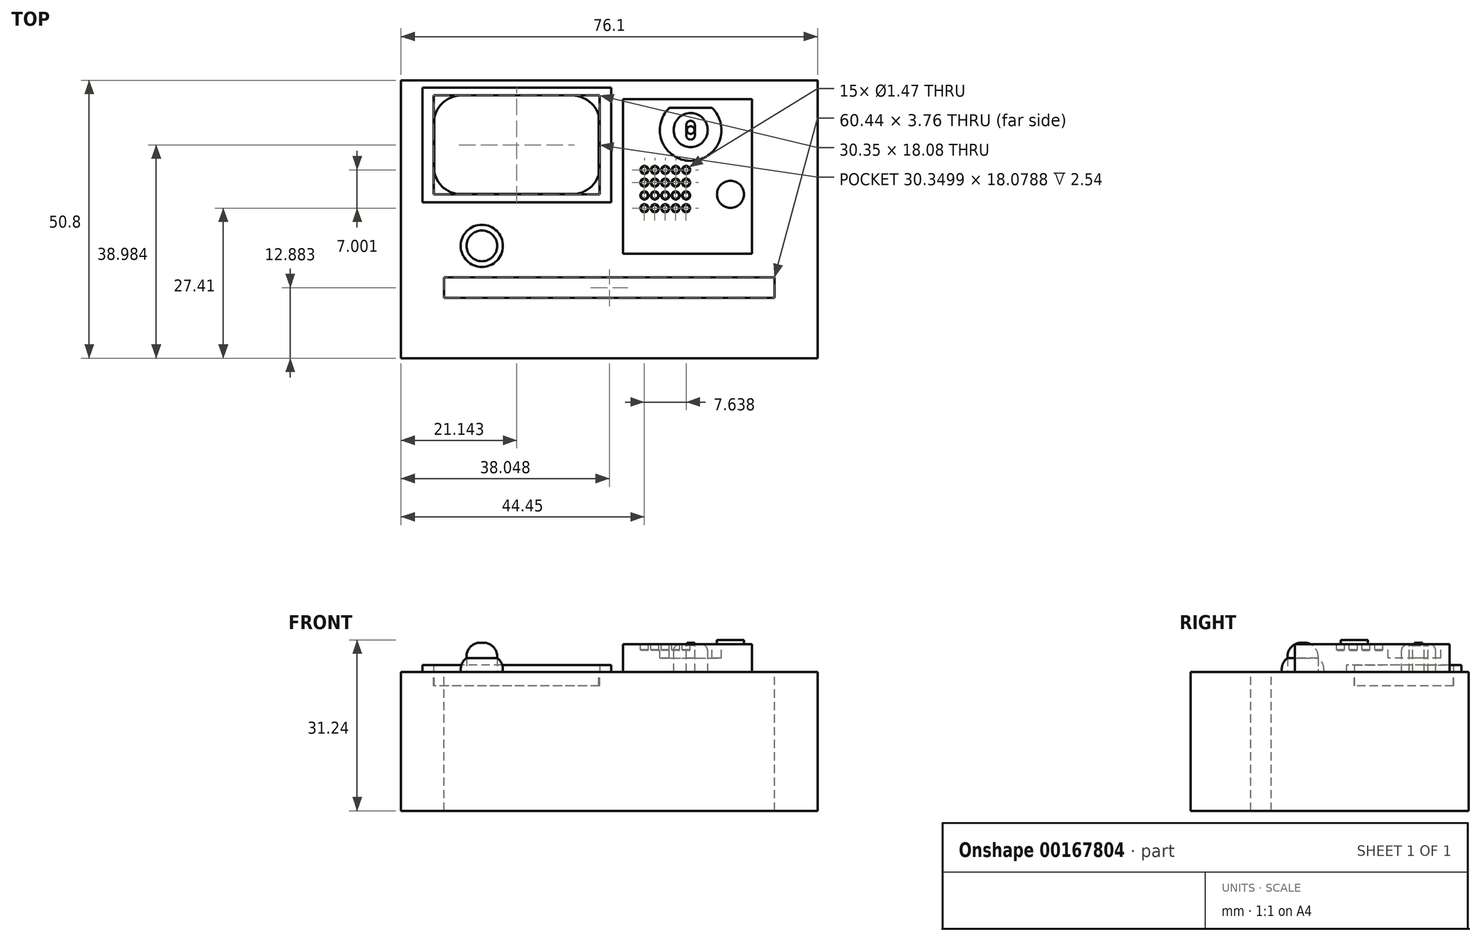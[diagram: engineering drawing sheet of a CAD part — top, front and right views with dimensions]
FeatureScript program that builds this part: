
annotation { "Feature Type Name" : "Feature", "Feature Type Description" : "" }
export const myFeature = defineFeature(function(context is Context, id is Id, definition is map)
    precondition{}
    {
        {
            var Q0;
            Q0=qCreatedBy(makeId("Front.planeOp"),FACE);
            var sketch = newSketch(context, id + "F0", { "sketchPlane" : qUnion([Q0])});
            skLineSegment(sketch, "E0.bottom", {"start": v(0, 0) * mm, "end": v(76.1, 0) * mm});
            skLineSegment(sketch, "E0.top", {"start": v(0, 25.4) * mm, "end": v(76.1, 25.4) * mm});
            skLineSegment(sketch, "E0.left", {"start": v(0, 0) * mm, "end": v(0, 25.4) * mm});
            skLineSegment(sketch, "E0.right", {"start": v(76.1, 0) * mm, "end": v(76.1, 25.4) * mm});
            skSolve(sketch);
        }
        {
            var Q0;
            Q0=makeQuery(id+"F0.imprint","IMPRINT",FACE,{"disambiguationData":[TD([[makeQuery(id+"F0.imprint","IMPRINT",EDGE,{"derivedFrom":sQuery(id+"F0.wireOp",EDGE,"E0.bottom")}),1.0]])]});
            extrude(context, id + "F1", {"entities" : qUnion([Q0]), "depth" : 50.8 * mm});
        }
        {
            var Q0;
            Q0=makeQuery(id+"F1.opExtrude","SWEPT_FACE",FACE,{"disambiguationData":[OSD([sQuery(id+"F0.wireOp",EDGE,"E0.top")])]});
            var sketch = newSketch(context, id + "F2", { "sketchPlane" : qUnion([Q0])});
            skLineSegment(sketch, "E1.bottom", {"start": v(7.83, -36.04) * mm, "end": v(68.27, -36.04) * mm});
            skLineSegment(sketch, "E1.top", {"start": v(7.83, -39.8) * mm, "end": v(68.27, -39.8) * mm});
            skLineSegment(sketch, "E1.left", {"start": v(7.83, -36.04) * mm, "end": v(7.83, -39.8) * mm});
            skLineSegment(sketch, "E1.right", {"start": v(68.27, -36.04) * mm, "end": v(68.27, -39.8) * mm});
            skLineSegment(sketch, "E2.bottom", {"start": v(64.1, -3.47) * mm, "end": v(40.54, -3.47) * mm});
            skLineSegment(sketch, "E2.top", {"start": v(64.1, -31.7) * mm, "end": v(40.54, -31.7) * mm});
            skLineSegment(sketch, "E2.left", {"start": v(64.1, -3.47) * mm, "end": v(64.1, -31.7) * mm});
            skLineSegment(sketch, "E2.right", {"start": v(40.54, -3.47) * mm, "end": v(40.54, -31.7) * mm});
            skCircle(sketch, "E3", {"center": v(14.76, -30.27) * mm, "radius": 3.85 * mm});
            skCircle(sketch, "E4", {"center": v(14.76, -30.27) * mm, "radius": 2.8 * mm});
            skSolve(sketch);
        }
        {
            var Q0;
            Q0=makeQuery(id+"F2.imprint","IMPRINT",FACE,{"disambiguationData":[TD([[makeQuery(id+"F2.imprint","IMPRINT",EDGE,{"derivedFrom":sQuery(id+"F2.wireOp",EDGE,"E1.bottom")}),-1.0]])]});
            extrude(context, id + "F3", {"entities" : qUnion([Q0]), "operationType" : NewBodyOperationType.REMOVE, "oppositeDirection" : true, "depth" : 63.5 * mm});
        }
        {
            var Q0;
            Q0=makeQuery(id+"F2.imprint","IMPRINT",FACE,{"disambiguationData":[TD([[makeQuery(id+"F2.imprint","IMPRINT",EDGE,{"derivedFrom":sQuery(id+"F2.wireOp",EDGE,"E3")}),1.0]])]});
            extrude(context, id + "F4", {"entities" : qUnion([Q0]), "depth" : 2.54 * mm});
        }
        {
            var Q0;
            Q0=makeQuery(id+"F2.imprint","IMPRINT",FACE,{"disambiguationData":[TD([[makeQuery(id+"F2.imprint","IMPRINT",EDGE,{"derivedFrom":sQuery(id+"F2.wireOp",EDGE,"DDiFx37W-qfiJ-qIsS-ybes-nbQmEh9gElsI")}),1.0]])]});
            var Q1;
            Q1=makeQuery(id+"F2.imprint","IMPRINT",FACE,{"disambiguationData":[TD([[makeQuery(id+"F2.imprint","IMPRINT",EDGE,{"derivedFrom":sQuery(id+"F2.wireOp",EDGE,"E4")}),1.0]])]});
            extrude(context, id + "F5", {"entities" : qUnion([Q0, Q1]), "depth" : 5.33 * mm});
        }
        {
            var Q0;
            Q0=makeQuery(id+"F5.opExtrude","CAP_EDGE",EDGE,{"disambiguationData":[OSD([sQuery(id+"F2.wireOp",EDGE,"DDiFx37W-qfiJ-qIsS-ybes-nbQmEh9gElsI")])],"isStart":false});
            var Q1;
            Q1=makeQuery(id+"F4.opExtrude","CAP_EDGE",EDGE,{"disambiguationData":[OSD([sQuery(id+"F2.wireOp",EDGE,"E3")])],"isStart":false});
            fillet(context, id + "F6", {"entities" : qUnion([Q0, Q1]), "radius" : 2.54 * mm, "tangentPropagation" : true, "allowEdgeOverflow" : false});
        }
        {
            var Q0;
            Q0=makeQuery(id+"F2.imprint","IMPRINT",FACE,{"disambiguationData":[TD([[makeQuery(id+"F2.imprint","IMPRINT",EDGE,{"derivedFrom":sQuery(id+"F2.wireOp",EDGE,"E2.bottom")}),1.0]])]});
            extrude(context, id + "F7", {"entities" : qUnion([Q0]), "depth" : 5.08 * mm});
        }
        {
            var Q0;
            Q0=makeQuery(id+"F7.opExtrude","CAP_FACE",FACE,{"disambiguationData":[OSD([sQuery(id+"F2.wireOp",EDGE,"E2.bottom"),sQuery(id+"F2.wireOp",EDGE,"E2.top"),sQuery(id+"F2.wireOp",EDGE,"E2.left"),sQuery(id+"F2.wireOp",EDGE,"E2.right")])],"isStart":false});
            var sketch = newSketch(context, id + "F8", { "sketchPlane" : qUnion([Q0])});
            skCircle(sketch, "E5", {"center": v(44.47, -16.39) * mm, "radius": 0.74 * mm});
            skCircle(sketch, "E6.1.0.0", {"center": v(46.37, -16.39) * mm, "radius": 0.74 * mm});
            skCircle(sketch, "E6.2.0.0", {"center": v(48.28, -16.39) * mm, "radius": 0.74 * mm});
            skCircle(sketch, "E6.3.0.0", {"center": v(50.18, -16.39) * mm, "radius": 0.74 * mm});
            skCircle(sketch, "E6.4.0.0", {"center": v(52.09, -16.39) * mm, "radius": 0.74 * mm});
            skLineSegment(sketch, "E6.direction1", {"start": v(44.47, -16.39) * mm, "end": v(46.37, -16.39) * mm, "construction": true});
            skCircle(sketch, "E7", {"center": v(44.45, -18.72) * mm, "radius": 0.74 * mm});
            skCircle(sketch, "E8.1.0.0", {"center": v(46.36, -18.72) * mm, "radius": 0.74 * mm});
            skCircle(sketch, "E8.2.0.0", {"center": v(48.26, -18.72) * mm, "radius": 0.74 * mm});
            skCircle(sketch, "E8.3.0.0", {"center": v(50.17, -18.72) * mm, "radius": 0.74 * mm});
            skCircle(sketch, "E8.4.0.0", {"center": v(52.07, -18.72) * mm, "radius": 0.74 * mm});
            skLineSegment(sketch, "E8.direction1", {"start": v(44.45, -18.72) * mm, "end": v(46.36, -18.72) * mm, "construction": true});
            skPoint(sketch, "E9.center.orphan", {"position": v(44.45, -21.05) * mm});
            skCircle(sketch, "E10", {"center": v(44.45, -21.05) * mm, "radius": 0.74 * mm});
            skPoint(sketch, "E11.1.0.0", {"position": v(46.36, -21.05) * mm});
            skCircle(sketch, "E11.1.0.1", {"center": v(46.36, -21.05) * mm, "radius": 0.74 * mm});
            skPoint(sketch, "E11.2.0.0", {"position": v(48.26, -21.05) * mm});
            skCircle(sketch, "E11.2.0.1", {"center": v(48.26, -21.05) * mm, "radius": 0.74 * mm});
            skLineSegment(sketch, "E11.direction1", {"start": v(44.45, -21.05) * mm, "end": v(46.36, -21.05) * mm, "construction": true});
            skPoint(sketch, "E12.0.3.0", {"position": v(50.17, -21.05) * mm});
            skCircle(sketch, "E12.1.3.0", {"center": v(50.17, -21.05) * mm, "radius": 0.74 * mm});
            skPoint(sketch, "E12.0.4.0", {"position": v(52.07, -21.05) * mm});
            skCircle(sketch, "E12.1.4.0", {"center": v(52.07, -21.05) * mm, "radius": 0.74 * mm});
            skCircle(sketch, "E13", {"center": v(44.45, -23.4) * mm, "radius": 0.74 * mm});
            skCircle(sketch, "E14.1.0.0", {"center": v(46.36, -23.4) * mm, "radius": 0.74 * mm});
            skCircle(sketch, "E14.2.0.0", {"center": v(48.26, -23.4) * mm, "radius": 0.74 * mm});
            skCircle(sketch, "E14.3.0.0", {"center": v(50.17, -23.4) * mm, "radius": 0.74 * mm});
            skCircle(sketch, "E14.4.0.0", {"center": v(52.07, -23.4) * mm, "radius": 0.74 * mm});
            skLineSegment(sketch, "E14.direction1", {"start": v(44.45, -23.4) * mm, "end": v(46.36, -23.4) * mm, "construction": true});
            skCircle(sketch, "E15", {"center": v(60.19, -20.84) * mm, "radius": 2.47 * mm});
            skLineSegment(sketch, "E16", {"start": v(49.01, -5.06) * mm, "end": v(56.8, -5.06) * mm});
            skArc(sketch, "E17", {"start": v(49.01, -5.06) * mm, "mid": v(52.9, -14.73) * mm, "end": v(56.8, -5.06) * mm});
            skCircle(sketch, "E18", {"center": v(52.9, -9.1) * mm, "radius": 3.11 * mm});
            skPoint(sketch, "E19.start.orphan", {"position": v(53.3, -7.58) * mm});
            skPoint(sketch, "E20.end.orphan", {"position": v(53.3, -10.17) * mm});
            skPoint(sketch, "E20.start.orphan", {"position": v(52.14, -10.17) * mm});
            skLineSegment(sketch, "E21", {"start": v(49.8, -9.14) * mm, "end": v(56.02, -9.14) * mm});
            skLineSegment(sketch, "E22", {"start": v(52.1, -9.14) * mm, "end": v(52.1, -10.17) * mm});
            skPoint(sketch, "E23.orphan", {"position": v(53.39, -7.58) * mm});
            skPoint(sketch, "E24.start.orphan", {"position": v(53.39, -10.17) * mm});
            skLineSegment(sketch, "E25", {"start": v(53.67, -9.14) * mm, "end": v(53.67, -10.17) * mm});
            skPoint(sketch, "E26.orphan", {"position": v(53.67, -7.58) * mm});
            skArc(sketch, "E27", {"start": v(52.1, -10.17) * mm, "mid": v(52.9, -10.85) * mm, "end": v(53.67, -10.17) * mm});
            skLineSegment(sketch, "E28", {"start": v(52.1, -9.14) * mm, "end": v(52.1, -8.1) * mm});
            skLineSegment(sketch, "E29", {"start": v(53.67, -9.14) * mm, "end": v(53.67, -8.1) * mm});
            skArc(sketch, "E30", {"start": v(53.67, -8.1) * mm, "mid": v(52.89, -7.41) * mm, "end": v(52.1, -8.1) * mm});
            skCircle(sketch, "E31", {"center": v(52.9, -9.1) * mm, "radius": 0.7 * mm});
            skSolve(sketch);
        }
        {
            var Q0;
            Q0=makeQuery(id+"F8.imprint","IMPRINT",FACE,{"disambiguationData":[TD([[makeQuery(id+"F8.imprint","IMPRINT",EDGE,{"derivedFrom":sQuery(id+"F8.wireOp",EDGE,"E5")}),1.0]])]});
            var Q1;
            Q1=makeQuery(id+"F8.imprint","IMPRINT",FACE,{"disambiguationData":[TD([[makeQuery(id+"F8.imprint","IMPRINT",EDGE,{"derivedFrom":sQuery(id+"F8.wireOp",EDGE,"E7")}),1.0]])]});
            var Q2;
            Q2=makeQuery(id+"F8.imprint","IMPRINT",FACE,{"disambiguationData":[TD([[makeQuery(id+"F8.imprint","IMPRINT",EDGE,{"derivedFrom":sQuery(id+"F8.wireOp",EDGE,"E6.1.0.0")}),1.0]])]});
            var Q3;
            Q3=makeQuery(id+"F8.imprint","IMPRINT",FACE,{"disambiguationData":[TD([[makeQuery(id+"F8.imprint","IMPRINT",EDGE,{"derivedFrom":sQuery(id+"F8.wireOp",EDGE,"E6.2.0.0")}),1.0]])]});
            var Q4;
            Q4=makeQuery(id+"F8.imprint","IMPRINT",FACE,{"disambiguationData":[TD([[makeQuery(id+"F8.imprint","IMPRINT",EDGE,{"derivedFrom":sQuery(id+"F8.wireOp",EDGE,"E6.3.0.0")}),1.0]])]});
            var Q5;
            Q5=makeQuery(id+"F8.imprint","IMPRINT",FACE,{"disambiguationData":[TD([[makeQuery(id+"F8.imprint","IMPRINT",EDGE,{"derivedFrom":sQuery(id+"F8.wireOp",EDGE,"E6.4.0.0")}),1.0]])]});
            var Q6;
            Q6=makeQuery(id+"F8.imprint","IMPRINT",FACE,{"disambiguationData":[TD([[makeQuery(id+"F8.imprint","IMPRINT",EDGE,{"derivedFrom":sQuery(id+"F8.wireOp",EDGE,"E8.4.0.0")}),1.0]])]});
            var Q7;
            Q7=makeQuery(id+"F8.imprint","IMPRINT",FACE,{"disambiguationData":[TD([[makeQuery(id+"F8.imprint","IMPRINT",EDGE,{"derivedFrom":sQuery(id+"F8.wireOp",EDGE,"E8.3.0.0")}),1.0]])]});
            var Q8;
            Q8=makeQuery(id+"F8.imprint","IMPRINT",FACE,{"disambiguationData":[TD([[makeQuery(id+"F8.imprint","IMPRINT",EDGE,{"derivedFrom":sQuery(id+"F8.wireOp",EDGE,"E8.2.0.0")}),1.0]])]});
            var Q9;
            Q9=makeQuery(id+"F8.imprint","IMPRINT",FACE,{"disambiguationData":[TD([[makeQuery(id+"F8.imprint","IMPRINT",EDGE,{"derivedFrom":sQuery(id+"F8.wireOp",EDGE,"E8.1.0.0")}),1.0]])]});
            var Q10;
            Q10=makeQuery(id+"F8.imprint","IMPRINT",FACE,{"disambiguationData":[TD([[makeQuery(id+"F8.imprint","IMPRINT",EDGE,{"derivedFrom":sQuery(id+"F8.wireOp",EDGE,"E10")}),1.0]])]});
            var Q11;
            Q11=makeQuery(id+"F8.imprint","IMPRINT",FACE,{"disambiguationData":[TD([[makeQuery(id+"F8.imprint","IMPRINT",EDGE,{"derivedFrom":sQuery(id+"F8.wireOp",EDGE,"E11.1.0.1")}),1.0]])]});
            var Q12;
            Q12=makeQuery(id+"F8.imprint","IMPRINT",FACE,{"disambiguationData":[TD([[makeQuery(id+"F8.imprint","IMPRINT",EDGE,{"derivedFrom":sQuery(id+"F8.wireOp",EDGE,"E11.2.0.1")}),1.0]])]});
            var Q13;
            Q13=makeQuery(id+"F8.imprint","IMPRINT",FACE,{"disambiguationData":[TD([[makeQuery(id+"F8.imprint","IMPRINT",EDGE,{"derivedFrom":sQuery(id+"F8.wireOp",EDGE,"E12.1.3.0")}),1.0]])]});
            var Q14;
            Q14=makeQuery(id+"F8.imprint","IMPRINT",FACE,{"disambiguationData":[TD([[makeQuery(id+"F8.imprint","IMPRINT",EDGE,{"derivedFrom":sQuery(id+"F8.wireOp",EDGE,"E12.1.4.0")}),1.0]])]});
            var Q15;
            Q15=makeQuery(id+"F8.imprint","IMPRINT",FACE,{"disambiguationData":[TD([[makeQuery(id+"F8.imprint","IMPRINT",EDGE,{"derivedFrom":sQuery(id+"F8.wireOp",EDGE,"E14.4.0.0")}),1.0]])]});
            var Q16;
            Q16=makeQuery(id+"F8.imprint","IMPRINT",FACE,{"disambiguationData":[TD([[makeQuery(id+"F8.imprint","IMPRINT",EDGE,{"derivedFrom":sQuery(id+"F8.wireOp",EDGE,"E14.3.0.0")}),1.0]])]});
            var Q17;
            Q17=makeQuery(id+"F8.imprint","IMPRINT",FACE,{"disambiguationData":[TD([[makeQuery(id+"F8.imprint","IMPRINT",EDGE,{"derivedFrom":sQuery(id+"F8.wireOp",EDGE,"E14.2.0.0")}),1.0]])]});
            var Q18;
            Q18=makeQuery(id+"F8.imprint","IMPRINT",FACE,{"disambiguationData":[TD([[makeQuery(id+"F8.imprint","IMPRINT",EDGE,{"derivedFrom":sQuery(id+"F8.wireOp",EDGE,"E14.1.0.0")}),1.0]])]});
            var Q19;
            Q19=makeQuery(id+"F8.imprint","IMPRINT",FACE,{"disambiguationData":[TD([[makeQuery(id+"F8.imprint","IMPRINT",EDGE,{"derivedFrom":sQuery(id+"F8.wireOp",EDGE,"E13")}),1.0]])]});
            extrude(context, id + "F9", {"entities" : qUnion([Q0, Q1, Q2, Q3, Q4, Q5, Q6, Q7, Q8, Q9, Q10, Q11, Q12, Q13, Q14, Q15, Q16, Q17, Q18, Q19]), "operationType" : NewBodyOperationType.REMOVE, "oppositeDirection" : true, "depth" : 1.17 * mm});
        }
        {
            var Q0;
            Q0=makeQuery(id+"F9.boolean.opBoolean","COPY",EDGE,{"derivedFrom":makeQuery(id+"F9.opExtrude","CAP_EDGE",EDGE,{"disambiguationData":[OSD([sQuery(id+"F8.wireOp",EDGE,"E5")])],"isStart":true})});
            var Q1;
            Q1=makeQuery(id+"F9.boolean.opBoolean","COPY",EDGE,{"derivedFrom":makeQuery(id+"F9.opExtrude","CAP_EDGE",EDGE,{"disambiguationData":[OSD([sQuery(id+"F8.wireOp",EDGE,"E6.1.0.0")])],"isStart":true})});
            var Q2;
            Q2=makeQuery(id+"F9.boolean.opBoolean","COPY",FACE,{"derivedFrom":makeQuery(id+"F9.opExtrude","CAP_FACE",FACE,{"disambiguationData":[OSD([sQuery(id+"F8.wireOp",EDGE,"E6.2.0.0")])],"isStart":false})});
            var Q3;
            Q3=makeQuery(id+"F9.boolean.opBoolean","COPY",FACE,{"derivedFrom":makeQuery(id+"F9.opExtrude","CAP_FACE",FACE,{"disambiguationData":[OSD([sQuery(id+"F8.wireOp",EDGE,"E6.3.0.0")])],"isStart":false})});
            var Q4;
            Q4=makeQuery(id+"F9.boolean.opBoolean","COPY",FACE,{"derivedFrom":makeQuery(id+"F9.opExtrude","CAP_FACE",FACE,{"disambiguationData":[OSD([sQuery(id+"F8.wireOp",EDGE,"E6.1.0.0")])],"isStart":false})});
            var Q5;
            Q5=makeQuery(id+"F9.boolean.opBoolean","COPY",FACE,{"derivedFrom":makeQuery(id+"F9.opExtrude","CAP_FACE",FACE,{"disambiguationData":[OSD([sQuery(id+"F8.wireOp",EDGE,"E5")])],"isStart":false})});
            var Q6;
            Q6=makeQuery(id+"F9.boolean.opBoolean","COPY",EDGE,{"derivedFrom":makeQuery(id+"F9.opExtrude","CAP_EDGE",EDGE,{"disambiguationData":[OSD([sQuery(id+"F8.wireOp",EDGE,"E6.2.0.0")])],"isStart":true})});
            var Q7;
            Q7=makeQuery(id+"F9.boolean.opBoolean","COPY",EDGE,{"derivedFrom":makeQuery(id+"F9.opExtrude","CAP_EDGE",EDGE,{"disambiguationData":[OSD([sQuery(id+"F8.wireOp",EDGE,"E6.3.0.0")])],"isStart":true})});
            var Q8;
            Q8=makeQuery(id+"F9.boolean.opBoolean","COPY",FACE,{"derivedFrom":makeQuery(id+"F9.opExtrude","CAP_FACE",FACE,{"disambiguationData":[OSD([sQuery(id+"F8.wireOp",EDGE,"E6.4.0.0")])],"isStart":false})});
            var Q9;
            Q9=makeQuery(id+"F9.boolean.opBoolean","COPY",EDGE,{"derivedFrom":makeQuery(id+"F9.opExtrude","CAP_EDGE",EDGE,{"disambiguationData":[OSD([sQuery(id+"F8.wireOp",EDGE,"E6.4.0.0")])],"isStart":true})});
            var Q10;
            Q10=makeQuery(id+"F9.boolean.opBoolean","COPY",EDGE,{"derivedFrom":makeQuery(id+"F9.opExtrude","CAP_EDGE",EDGE,{"disambiguationData":[OSD([sQuery(id+"F8.wireOp",EDGE,"E7")])],"isStart":true})});
            var Q11;
            Q11=makeQuery(id+"F9.boolean.opBoolean","COPY",FACE,{"derivedFrom":makeQuery(id+"F9.opExtrude","CAP_FACE",FACE,{"disambiguationData":[OSD([sQuery(id+"F8.wireOp",EDGE,"E7")])],"isStart":false})});
            var Q12;
            Q12=makeQuery(id+"F9.boolean.opBoolean","COPY",EDGE,{"derivedFrom":makeQuery(id+"F9.opExtrude","CAP_EDGE",EDGE,{"disambiguationData":[OSD([sQuery(id+"F8.wireOp",EDGE,"E8.1.0.0")])],"isStart":true})});
            var Q13;
            Q13=makeQuery(id+"F9.boolean.opBoolean","COPY",FACE,{"derivedFrom":makeQuery(id+"F9.opExtrude","CAP_FACE",FACE,{"disambiguationData":[OSD([sQuery(id+"F8.wireOp",EDGE,"E8.1.0.0")])],"isStart":false})});
            var Q14;
            Q14=makeQuery(id+"F9.boolean.opBoolean","COPY",FACE,{"derivedFrom":makeQuery(id+"F9.opExtrude","CAP_FACE",FACE,{"disambiguationData":[OSD([sQuery(id+"F8.wireOp",EDGE,"E8.2.0.0")])],"isStart":false})});
            var Q15;
            Q15=makeQuery(id+"F9.boolean.opBoolean","COPY",EDGE,{"derivedFrom":makeQuery(id+"F9.opExtrude","CAP_EDGE",EDGE,{"disambiguationData":[OSD([sQuery(id+"F8.wireOp",EDGE,"E8.2.0.0")])],"isStart":true})});
            var Q16;
            Q16=makeQuery(id+"F9.boolean.opBoolean","COPY",FACE,{"derivedFrom":makeQuery(id+"F9.opExtrude","CAP_FACE",FACE,{"disambiguationData":[OSD([sQuery(id+"F8.wireOp",EDGE,"E8.3.0.0")])],"isStart":false})});
            var Q17;
            Q17=makeQuery(id+"F9.boolean.opBoolean","COPY",EDGE,{"derivedFrom":makeQuery(id+"F9.opExtrude","CAP_EDGE",EDGE,{"disambiguationData":[OSD([sQuery(id+"F8.wireOp",EDGE,"E8.3.0.0")])],"isStart":true})});
            var Q18;
            Q18=makeQuery(id+"F9.boolean.opBoolean","COPY",FACE,{"derivedFrom":makeQuery(id+"F9.opExtrude","CAP_FACE",FACE,{"disambiguationData":[OSD([sQuery(id+"F8.wireOp",EDGE,"E8.4.0.0")])],"isStart":false})});
            var Q19;
            Q19=makeQuery(id+"F9.boolean.opBoolean","COPY",EDGE,{"derivedFrom":makeQuery(id+"F9.opExtrude","CAP_EDGE",EDGE,{"disambiguationData":[OSD([sQuery(id+"F8.wireOp",EDGE,"E8.4.0.0")])],"isStart":true})});
            var Q20;
            Q20=makeQuery(id+"F9.boolean.opBoolean","COPY",FACE,{"derivedFrom":makeQuery(id+"F9.opExtrude","CAP_FACE",FACE,{"disambiguationData":[OSD([sQuery(id+"F8.wireOp",EDGE,"E12.1.4.0")])],"isStart":false})});
            var Q21;
            Q21=makeQuery(id+"F9.boolean.opBoolean","COPY",EDGE,{"derivedFrom":makeQuery(id+"F9.opExtrude","CAP_EDGE",EDGE,{"disambiguationData":[OSD([sQuery(id+"F8.wireOp",EDGE,"E12.1.4.0")])],"isStart":true})});
            var Q22;
            Q22=makeQuery(id+"F9.boolean.opBoolean","COPY",FACE,{"derivedFrom":makeQuery(id+"F9.opExtrude","CAP_FACE",FACE,{"disambiguationData":[OSD([sQuery(id+"F8.wireOp",EDGE,"E12.1.3.0")])],"isStart":false})});
            var Q23;
            Q23=makeQuery(id+"F9.boolean.opBoolean","COPY",EDGE,{"derivedFrom":makeQuery(id+"F9.opExtrude","CAP_EDGE",EDGE,{"disambiguationData":[OSD([sQuery(id+"F8.wireOp",EDGE,"E12.1.3.0")])],"isStart":true})});
            var Q24;
            Q24=makeQuery(id+"F9.boolean.opBoolean","COPY",FACE,{"derivedFrom":makeQuery(id+"F9.opExtrude","CAP_FACE",FACE,{"disambiguationData":[OSD([sQuery(id+"F8.wireOp",EDGE,"E11.2.0.1")])],"isStart":false})});
            var Q25;
            Q25=makeQuery(id+"F9.boolean.opBoolean","COPY",EDGE,{"derivedFrom":makeQuery(id+"F9.opExtrude","CAP_EDGE",EDGE,{"disambiguationData":[OSD([sQuery(id+"F8.wireOp",EDGE,"E11.2.0.1")])],"isStart":true})});
            var Q26;
            Q26=makeQuery(id+"F9.boolean.opBoolean","COPY",FACE,{"derivedFrom":makeQuery(id+"F9.opExtrude","CAP_FACE",FACE,{"disambiguationData":[OSD([sQuery(id+"F8.wireOp",EDGE,"E11.1.0.1")])],"isStart":false})});
            var Q27;
            Q27=makeQuery(id+"F9.boolean.opBoolean","COPY",EDGE,{"derivedFrom":makeQuery(id+"F9.opExtrude","CAP_EDGE",EDGE,{"disambiguationData":[OSD([sQuery(id+"F8.wireOp",EDGE,"E11.1.0.1")])],"isStart":true})});
            var Q28;
            Q28=makeQuery(id+"F9.boolean.opBoolean","COPY",FACE,{"derivedFrom":makeQuery(id+"F9.opExtrude","CAP_FACE",FACE,{"disambiguationData":[OSD([sQuery(id+"F8.wireOp",EDGE,"E10")])],"isStart":false})});
            var Q29;
            Q29=makeQuery(id+"F9.boolean.opBoolean","COPY",EDGE,{"derivedFrom":makeQuery(id+"F9.opExtrude","CAP_EDGE",EDGE,{"disambiguationData":[OSD([sQuery(id+"F8.wireOp",EDGE,"E10")])],"isStart":true})});
            var Q30;
            Q30=makeQuery(id+"F9.boolean.opBoolean","COPY",FACE,{"derivedFrom":makeQuery(id+"F9.opExtrude","CAP_FACE",FACE,{"disambiguationData":[OSD([sQuery(id+"F8.wireOp",EDGE,"E13")])],"isStart":false})});
            var Q31;
            Q31=makeQuery(id+"F9.boolean.opBoolean","COPY",EDGE,{"derivedFrom":makeQuery(id+"F9.opExtrude","CAP_EDGE",EDGE,{"disambiguationData":[OSD([sQuery(id+"F8.wireOp",EDGE,"E13")])],"isStart":true})});
            var Q32;
            Q32=makeQuery(id+"F9.boolean.opBoolean","COPY",FACE,{"derivedFrom":makeQuery(id+"F9.opExtrude","CAP_FACE",FACE,{"disambiguationData":[OSD([sQuery(id+"F8.wireOp",EDGE,"E14.1.0.0")])],"isStart":false})});
            var Q33;
            Q33=makeQuery(id+"F9.boolean.opBoolean","COPY",EDGE,{"derivedFrom":makeQuery(id+"F9.opExtrude","CAP_EDGE",EDGE,{"disambiguationData":[OSD([sQuery(id+"F8.wireOp",EDGE,"E14.1.0.0")])],"isStart":true})});
            var Q34;
            Q34=makeQuery(id+"F9.boolean.opBoolean","COPY",EDGE,{"derivedFrom":makeQuery(id+"F9.opExtrude","CAP_EDGE",EDGE,{"disambiguationData":[OSD([sQuery(id+"F8.wireOp",EDGE,"E14.2.0.0")])],"isStart":true})});
            var Q35;
            Q35=makeQuery(id+"F9.boolean.opBoolean","COPY",FACE,{"derivedFrom":makeQuery(id+"F9.opExtrude","CAP_FACE",FACE,{"disambiguationData":[OSD([sQuery(id+"F8.wireOp",EDGE,"E14.2.0.0")])],"isStart":false})});
            var Q36;
            Q36=makeQuery(id+"F9.boolean.opBoolean","COPY",FACE,{"derivedFrom":makeQuery(id+"F9.opExtrude","CAP_FACE",FACE,{"disambiguationData":[OSD([sQuery(id+"F8.wireOp",EDGE,"E14.3.0.0")])],"isStart":false})});
            var Q37;
            Q37=makeQuery(id+"F9.boolean.opBoolean","COPY",EDGE,{"derivedFrom":makeQuery(id+"F9.opExtrude","CAP_EDGE",EDGE,{"disambiguationData":[OSD([sQuery(id+"F8.wireOp",EDGE,"E14.3.0.0")])],"isStart":true})});
            var Q38;
            Q38=makeQuery(id+"F9.boolean.opBoolean","COPY",FACE,{"derivedFrom":makeQuery(id+"F9.opExtrude","CAP_FACE",FACE,{"disambiguationData":[OSD([sQuery(id+"F8.wireOp",EDGE,"E14.4.0.0")])],"isStart":false})});
            var Q39;
            Q39=makeQuery(id+"F9.boolean.opBoolean","COPY",EDGE,{"derivedFrom":makeQuery(id+"F9.opExtrude","CAP_EDGE",EDGE,{"disambiguationData":[OSD([sQuery(id+"F8.wireOp",EDGE,"E14.4.0.0")])],"isStart":true})});
            chamfer(context, id + "F10", {"entities" : qUnion([Q0, Q1, Q2, Q3, Q4, Q5, Q6, Q7, Q8, Q9, Q10, Q11, Q12, Q13, Q14, Q15, Q16, Q17, Q18, Q19, Q20, Q21, Q22, Q23, Q24, Q25, Q26, Q27, Q28, Q29, Q30, Q31, Q32, Q33, Q34, Q35, Q36, Q37, Q38, Q39]), "width" : 0.13 * mm, "tangentPropagation" : true});
        }
        {
            var Q0;
            Q0=makeQuery(id+"F8.imprint","IMPRINT",FACE,{"disambiguationData":[TD([[makeQuery(id+"F8.imprint","IMPRINT",EDGE,{"derivedFrom":sQuery(id+"F8.wireOp",EDGE,"E15")}),1.0]])]});
            extrude(context, id + "F11", {"entities" : qUnion([Q0]), "depth" : 0.76 * mm});
        }
        {
            var Q0;
            Q0=makeQuery(id+"F8.imprint","IMPRINT",FACE,{"disambiguationData":[TD([[makeQuery(id+"F8.imprint","IMPRINT",EDGE,{"derivedFrom":sQuery(id+"F8.wireOp",EDGE,"E16")}),-1.0]])]});
            var Q1;
            Q1=makeQuery(id+"F8.imprint","IMPRINT",FACE,{"disambiguationData":[TD([[makeQuery(id+"F8.imprint","IMPRINT",EDGE,{"derivedFrom":sQuery(id+"F8.wireOp",EDGE,"E18")}),1.0]])]});
            extrude(context, id + "F12", {"entities" : qUnion([Q0, Q1]), "operationType" : NewBodyOperationType.REMOVE, "oppositeDirection" : true, "depth" : 2.54 * mm});
        }
        {
            var Q0;
            Q0=makeQuery(id+"F8.imprint","IMPRINT",FACE,{"disambiguationData":[TD([[makeQuery(id+"F8.imprint","IMPRINT",EDGE,{"derivedFrom":sQuery(id+"F8.wireOp",EDGE,"E18")}),1.0]])]});
            var Q1;
            {var subQ0=sQuery(id+"F8.wireOp",EDGE,"hfNGeZEo-kC2R-xQsO-6JbA-2QM3XA8GC7YY");Q1=makeQuery(id+"F8.imprint","IMPRINT",FACE,{"disambiguationData":[TD([[makeQuery(id+"F8.imprint","IMPRINT",EDGE,{"derivedFrom":subQ0}),-1.0]])]});}
            extrude(context, id + "F13", {"entities" : qUnion([Q0, Q1]), "oppositeDirection" : true, "depth" : 5.08 * mm});
        }
        {
            var Q0;
            Q0=makeQuery(id+"F13.opExtrude","CAP_EDGE",EDGE,{"disambiguationData":[OSD([sQuery(id+"F8.wireOp",EDGE,"E18")])],"isStart":true});
            var Q1;
            Q1=makeQuery(id+"F12.boolean.opBoolean","COPY",EDGE,{"derivedFrom":makeQuery(id+"F12.opExtrude","CAP_EDGE",EDGE,{"disambiguationData":[OSD([sQuery(id+"F8.wireOp",EDGE,"E18")])],"isStart":true})});
            fillet(context, id + "F14", {"entities" : qUnion([Q0, Q1]), "radius" : 1.27 * mm, "tangentPropagation" : true, "allowEdgeOverflow" : false});
        }
        {
            var Q0;
            {var subQ0=sQuery(id+"F8.wireOp",EDGE,"E28");Q0=makeQuery(id+"F8.imprint","IMPRINT",FACE,{"disambiguationData":[TD([[makeQuery(id+"F8.imprint","IMPRINT",EDGE,{"derivedFrom":subQ0}),-1.0]])]});}
            var Q1;
            {var subQ0=sQuery(id+"F8.wireOp",EDGE,"E22");Q1=makeQuery(id+"F8.imprint","IMPRINT",FACE,{"disambiguationData":[TD([[makeQuery(id+"F8.imprint","IMPRINT",EDGE,{"derivedFrom":subQ0}),1.0]])]});}
            var Q2;
            {var subQ0=sQuery(id+"F8.wireOp",EDGE,"E31");var subQ1=sQuery(id+"F8.wireOp",EDGE,"E21");var subQ2=makeQuery(id+"F8.imprint","INTERSECT",VERTEX,{"disambiguationData":[OD(0.0)],"derivedFrom":[subQ1,subQ0]});Q2=makeQuery(id+"F8.imprint","IMPRINT",FACE,{"disambiguationData":[TD([[makeQuery(id+"F8.imprint","IMPRINT",EDGE,{"disambiguationData":[TD([[subQ2,-1.0]])],"derivedFrom":subQ1}),-1.0]])]});}
            var Q3;
            {var subQ0=sQuery(id+"F8.wireOp",EDGE,"E31");var subQ1=sQuery(id+"F8.wireOp",EDGE,"E21");var subQ2=makeQuery(id+"F8.imprint","INTERSECT",VERTEX,{"disambiguationData":[OD(0.0)],"derivedFrom":[subQ1,subQ0]});Q3=makeQuery(id+"F8.imprint","IMPRINT",FACE,{"disambiguationData":[TD([[makeQuery(id+"F8.imprint","IMPRINT",EDGE,{"disambiguationData":[TD([[subQ2,-1.0]])],"derivedFrom":subQ1}),1.0]])]});}
            extrude(context, id + "F15", {"entities" : qUnion([Q0, Q1, Q2, Q3]), "operationType" : NewBodyOperationType.REMOVE, "oppositeDirection" : true, "depth" : 0.25 * mm});
        }
        {
            var Q0;
            {var subQ0=sQuery(id+"F8.wireOp",EDGE,"E31");var subQ1=sQuery(id+"F8.wireOp",EDGE,"E21");var subQ2=makeQuery(id+"F8.imprint","INTERSECT",VERTEX,{"disambiguationData":[OD(0.0)],"derivedFrom":[subQ1,subQ0]});Q0=makeQuery(id+"F8.imprint","IMPRINT",FACE,{"disambiguationData":[TD([[makeQuery(id+"F8.imprint","IMPRINT",EDGE,{"disambiguationData":[TD([[subQ2,-1.0]])],"derivedFrom":subQ1}),1.0]])]});}
            var Q1;
            {var subQ0=sQuery(id+"F8.wireOp",EDGE,"E31");var subQ1=sQuery(id+"F8.wireOp",EDGE,"E21");var subQ2=makeQuery(id+"F8.imprint","INTERSECT",VERTEX,{"disambiguationData":[OD(0.0)],"derivedFrom":[subQ1,subQ0]});Q1=makeQuery(id+"F8.imprint","IMPRINT",FACE,{"disambiguationData":[TD([[makeQuery(id+"F8.imprint","IMPRINT",EDGE,{"disambiguationData":[TD([[subQ2,-1.0]])],"derivedFrom":subQ1}),-1.0]])]});}
            extrude(context, id + "F16", {"entities" : qUnion([Q0, Q1]), "depth" : 0.25 * mm});
        }
        {
            var Q0;
            Q0=makeQuery(id+"F2.imprint","IMPRINT",FACE,{"disambiguationData":[TD([[makeQuery(id+"F2.imprint","IMPRINT",EDGE,{"derivedFrom":sQuery(id+"F2.wireOp",EDGE,"E1.bottom")}),1.0]])]});
            cPlane(context, id + "F17", {"entities" : qUnion([Q0]), "cplaneType" : CPlaneType.OFFSET, "offset" : 0 * mm, "width" : 152.4 * mm, "height" : 152.4 * mm});
        }
        {
            var Q0;
            Q0=qCreatedBy(id+"F17.planeOp",FACE);
            var sketch = newSketch(context, id + "F18", { "sketchPlane" : qUnion([Q0])});
            skPoint(sketch, "E32.middle", {"position": v(19.74, -8.66) * mm});
            skPoint(sketch, "E32.middle.positionSnap0", {"position": v(19.74, 4.04) * mm});
            skPoint(sketch, "E32.middle.positionSnap1", {"position": v(36.35, -8.66) * mm});
            skPoint(sketch, "E32.centerSnap0", {"position": v(19.74, 4.04) * mm});
            skPoint(sketch, "E32.centerSnap1", {"position": v(36.35, -8.66) * mm});
            skPoint(sketch, "E33.orphan", {"position": v(36.35, 4.04) * mm});
            skPoint(sketch, "E34.right.start.orphan", {"position": v(3.13, 4.04) * mm});
            skPoint(sketch, "E32.right.end.orphan", {"position": v(4.48, -4.08) * mm});
            skPoint(sketch, "E32.bottom.end.orphan", {"position": v(4.48, -13.25) * mm});
            skPoint(sketch, "E32.left.end.orphan", {"position": v(35, -4.08) * mm});
            skPoint(sketch, "E32.left.start.orphan", {"position": v(35, -13.25) * mm});
            skPoint(sketch, "E34.top.start.orphan", {"position": v(36.35, -21.36) * mm});
            skLineSegment(sketch, "E35.bottom", {"start": v(38.38, -1.33) * mm, "end": v(3.9, -1.33) * mm});
            skLineSegment(sketch, "E35.top", {"start": v(38.38, -22.3) * mm, "end": v(3.9, -22.3) * mm});
            skLineSegment(sketch, "E35.left", {"start": v(38.38, -1.33) * mm, "end": v(38.38, -22.3) * mm});
            skLineSegment(sketch, "E35.right", {"start": v(3.9, -1.33) * mm, "end": v(3.9, -22.3) * mm});
            skPoint(sketch, "E35.middle", {"position": v(21.14, -11.82) * mm});
            skLineSegment(sketch, "E36.bottom", {"start": v(36.32, -2.78) * mm, "end": v(5.97, -2.78) * mm});
            skLineSegment(sketch, "E36.top", {"start": v(36.32, -20.86) * mm, "end": v(5.97, -20.86) * mm});
            skLineSegment(sketch, "E36.left", {"start": v(36.32, -2.78) * mm, "end": v(36.32, -20.86) * mm});
            skLineSegment(sketch, "E36.right", {"start": v(5.97, -2.78) * mm, "end": v(5.97, -20.86) * mm});
            skSolve(sketch);
        }
        {
            var Q0;
            Q0=makeQuery(id+"F5.opExtrude","CAP_EDGE",EDGE,{"disambiguationData":[OSD([sQuery(id+"F2.wireOp",EDGE,"E4")])],"isStart":false});
            fillet(context, id + "F19", {"entities" : qUnion([Q0]), "radius" : 2.54 * mm, "tangentPropagation" : true, "allowEdgeOverflow" : false});
        }
        {
            var Q0;
            Q0=makeQuery(id+"F18.imprint","IMPRINT",FACE,{"disambiguationData":[TD([[makeQuery(id+"F18.imprint","IMPRINT",EDGE,{"derivedFrom":sQuery(id+"F18.wireOp",EDGE,"E35.bottom")}),1.0]])]});
            extrude(context, id + "F20", {"entities" : qUnion([Q0]), "depth" : 1.27 * mm});
        }
        {
            var Q0;
            Q0=makeQuery(id+"F20.opExtrude","SWEPT_EDGE",EDGE,{"disambiguationData":[OSD([sQuery(id+"F18.wireOp",EDGE,"E36.bottom"),sQuery(id+"F18.wireOp",EDGE,"E36.left")])]});
            var Q1;
            Q1=makeQuery(id+"F20.opExtrude","SWEPT_EDGE",EDGE,{"disambiguationData":[OSD([sQuery(id+"F18.wireOp",EDGE,"E36.bottom"),sQuery(id+"F18.wireOp",EDGE,"E36.right")])]});
            var Q2;
            Q2=makeQuery(id+"F20.opExtrude","SWEPT_EDGE",EDGE,{"disambiguationData":[OSD([sQuery(id+"F18.wireOp",EDGE,"E36.top"),sQuery(id+"F18.wireOp",EDGE,"E36.left")])]});
            var Q3;
            Q3=makeQuery(id+"F20.opExtrude","SWEPT_EDGE",EDGE,{"disambiguationData":[OSD([sQuery(id+"F18.wireOp",EDGE,"E36.top"),sQuery(id+"F18.wireOp",EDGE,"E36.right")])]});
            fillet(context, id + "F21", {"entities" : qUnion([Q0, Q1, Q2, Q3]), "radius" : 5.08 * mm, "tangentPropagation" : true, "allowEdgeOverflow" : false});
        }
        {
            var Q0;
            Q0=makeQuery(id+"F18.imprint","IMPRINT",FACE,{"disambiguationData":[TD([[makeQuery(id+"F18.imprint","IMPRINT",EDGE,{"derivedFrom":sQuery(id+"F18.wireOp",EDGE,"E36.bottom")}),1.0]])]});
            extrude(context, id + "F22", {"entities" : qUnion([Q0]), "operationType" : NewBodyOperationType.REMOVE, "oppositeDirection" : true, "depth" : 2.54 * mm});
        }
        {
            var Q0;
            Q0=makeQuery(id+"F18.imprint","IMPRINT",FACE,{"disambiguationData":[TD([[makeQuery(id+"F18.imprint","IMPRINT",EDGE,{"derivedFrom":sQuery(id+"F18.wireOp",EDGE,"E36.bottom")}),1.0]])]});
            cPlane(context, id + "F23", {"entities" : qUnion([Q0]), "cplaneType" : CPlaneType.OFFSET, "offset" : 0 * mm, "width" : 152.4 * mm, "height" : 152.4 * mm});
        }
        {
            var Q0;
            Q0=qCreatedBy(id+"F23.planeOp",FACE);
            var sketch = newSketch(context, id + "F24", { "sketchPlane" : qUnion([Q0])});
            skLineSegment(sketch, "E37.bottom", {"start": v(36.13, -2.72) * mm, "end": v(6.1, -2.72) * mm});
            skLineSegment(sketch, "E37.top", {"start": v(36.13, -20.8) * mm, "end": v(6.1, -20.8) * mm});
            skLineSegment(sketch, "E37.left", {"start": v(36.13, -2.72) * mm, "end": v(36.13, -20.8) * mm});
            skLineSegment(sketch, "E37.right", {"start": v(6.1, -2.72) * mm, "end": v(6.1, -20.8) * mm});
            skPoint(sketch, "E37.middle", {"position": v(21.11, -11.76) * mm});
            skSolve(sketch);
        }
        {
            var Q0;
            Q0=makeQuery(id+"F24.imprint","IMPRINT",FACE,{"disambiguationData":[TD([[makeQuery(id+"F24.imprint","IMPRINT",EDGE,{"derivedFrom":sQuery(id+"F24.wireOp",EDGE,"E37.bottom")}),1.0]])]});
            extrude(context, id + "F25", {"entities" : qUnion([Q0]), "oppositeDirection" : true, "depth" : 2.54 * mm});
        }
        {
            var Q0;
            Q0=makeQuery(id+"F1.opExtrude","CAP_FACE",FACE,{"disambiguationData":[OSD([sQuery(id+"F0.wireOp",EDGE,"E0.bottom"),sQuery(id+"F0.wireOp",EDGE,"E0.top"),sQuery(id+"F0.wireOp",EDGE,"E0.left"),sQuery(id+"F0.wireOp",EDGE,"E0.right")])],"isStart":false});
            cPlane(context, id + "F26", {"entities" : qUnion([Q0]), "cplaneType" : CPlaneType.OFFSET, "offset" : 0 * mm, "width" : 152.4 * mm, "height" : 152.4 * mm});
        }
        {
            var Q0;
            Q0=qCreatedBy(makeId("Front.planeOp"),FACE);
            var sketch = newSketch(context, id + "F27", { "sketchPlane" : qUnion([Q0])});
            skLineSegment(sketch, "E38.bottom", {"start": v(0, -18) * mm, "end": v(75.78, -18) * mm});
            skLineSegment(sketch, "E38.top", {"start": v(0, -75.94) * mm, "end": v(75.78, -75.94) * mm});
            skLineSegment(sketch, "E38.left", {"start": v(0, -18) * mm, "end": v(0, -75.94) * mm});
            skLineSegment(sketch, "E38.right", {"start": v(75.78, -18) * mm, "end": v(75.78, -75.94) * mm});
            skSolve(sketch);
        }
    });
